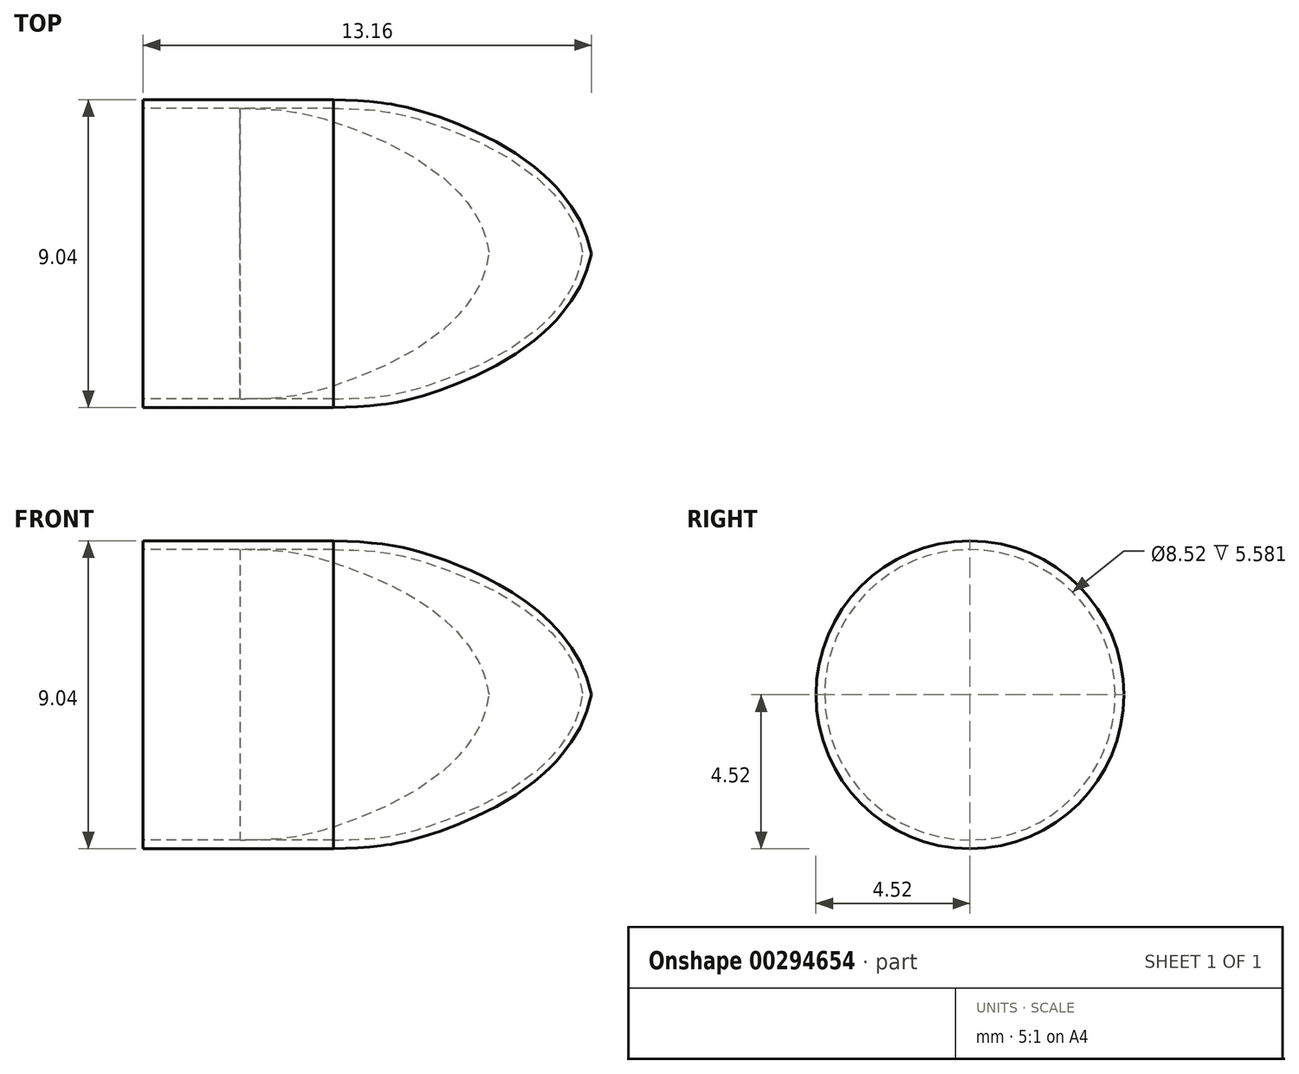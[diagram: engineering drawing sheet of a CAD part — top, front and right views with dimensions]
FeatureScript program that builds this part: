
annotation { "Feature Type Name" : "Feature", "Feature Type Description" : "" }
export const myFeature = defineFeature(function(context is Context, id is Id, definition is map)
    precondition{}
    {
        {
            var Q0;
            Q0=qCreatedBy(makeId("Front.planeOp"),FACE);
            var sketch = newSketch(context, id + "F0", { "sketchPlane" : qUnion([Q0])});
            skLineSegment(sketch, "E0", {"start": v(0, 0) * mm, "end": v(0, 4.51) * mm});
            skLineSegment(sketch, "E1", {"start": v(0, 4.51) * mm, "end": v(13.16, 4.51) * mm, "construction": true});
            skLineSegment(sketch, "E2", {"start": v(13.16, 4.51) * mm, "end": v(13.16, 0) * mm, "construction": true});
            skLineSegment(sketch, "E3", {"start": v(13.16, 0) * mm, "end": v(0, 0) * mm});
            skLineSegment(sketch, "E4", {"start": v(0, 0) * mm, "end": v(22.95, 0) * mm, "construction": true});
            skLineSegment(sketch, "E5", {"start": v(0, 4.51) * mm, "end": v(5.59, 4.51) * mm});
            skFitSpline(sketch, "E6", {"points": [v(5.59, 4.51) * mm, v(8.84, 3.96) * mm, v(13.16, 0) * mm], "startDerivative": vector(9.64, -0.25) * mm, "endDerivative": vector(2.57, -11.86) * mm});
            skPoint(sketch, "E7", {"position": v(13.16, 2.26) * mm});
            skFitSpline(sketch, "E8.0", {"points": [v(5.58, 4.26) * mm, v(5.98, 4.25) * mm, v(6.66, 4.22) * mm, v(7.36, 4.12) * mm, v(7.9, 4) * mm, v(8.34, 3.87) * mm, v(8.81, 3.7) * mm, v(9.52, 3.42) * mm, v(10.47, 2.97) * mm, v(11.56, 2.21) * mm, v(12.45, 1.23) * mm, v(12.81, 0.4) * mm, v(12.91, -0.05) * mm]});
            skLineSegment(sketch, "E9", {"start": v(5.58, 4.26) * mm, "end": v(0, 4.26) * mm});
            skSolve(sketch);
        }
        {
            var Q0;
            {var subQ4=sQuery(id+"F0.wireOp",EDGE,"E8.0");Q0=makeQuery(id+"F0.imprint","IMPRINT",FACE,{"disambiguationData":[TD([[makeQuery(id+"F0.imprint","IMPRINT",EDGE,{"derivedFrom":subQ4}),-1.0]])]});}
            var sketch = newSketch(context, id + "F1", { "sketchPlane" : qUnion([Q0])});
            skLineSegment(sketch, "E10", {"start": v(0, 0) * mm, "end": v(12.44, 0) * mm, "construction": true});
            skFitSpline(sketch, "E11.0.0", {"points": [v(10.17, -0.05) * mm, v(10.07, 0.4) * mm, v(9.7, 1.23) * mm, v(8.82, 2.21) * mm, v(7.72, 2.97) * mm, v(6.77, 3.42) * mm, v(6.07, 3.7) * mm, v(5.6, 3.87) * mm, v(5.16, 4) * mm, v(4.61, 4.12) * mm, v(3.92, 4.22) * mm, v(3.24, 4.25) * mm, v(2.84, 4.26) * mm]});
            skLineSegment(sketch, "E11.0.1", {"start": v(5.58, 4.26) * mm, "end": v(0, 4.26) * mm});
            skLineSegment(sketch, "E11.0.2", {"start": v(0, 4.26) * mm, "end": v(0, 0) * mm});
            skLineSegment(sketch, "E11.0.3", {"start": v(0, 0) * mm, "end": v(12.9, 0) * mm});
            skSolve(sketch);
        }
        {
            var Q0;
            {var subQ1=sQuery(id+"F0.wireOp",EDGE,"E5");Q0=makeQuery(id+"F0.imprint","IMPRINT",FACE,{"disambiguationData":[TD([[makeQuery(id+"F0.imprint","IMPRINT",EDGE,{"derivedFrom":subQ1}),-1.0]])]});}
            var Q1;
            Q1=sQuery(id+"F0.wireOp",EDGE,"E4");
            revolve(context, id + "F2", {"entities" : qUnion([Q0]), "axis" : qUnion([Q1]), "revolveType" : RevolveType.FULL});
        }
        {
            var Q0;
            Q0=makeQuery(id+"F1.imprint","IMPRINT",FACE,{"disambiguationData":[TD([[makeQuery(id+"F1.imprint","IMPRINT",EDGE,{"derivedFrom":sQuery(id+"F1.wireOp",EDGE,"E11.0.0")}),-1.0]])]});
            var Q1;
            Q1=sQuery(id+"F1.wireOp",EDGE,"E10");
            revolve(context, id + "F3", {"entities" : qUnion([Q0]), "axis" : qUnion([Q1]), "revolveType" : RevolveType.FULL});
        }
    });
